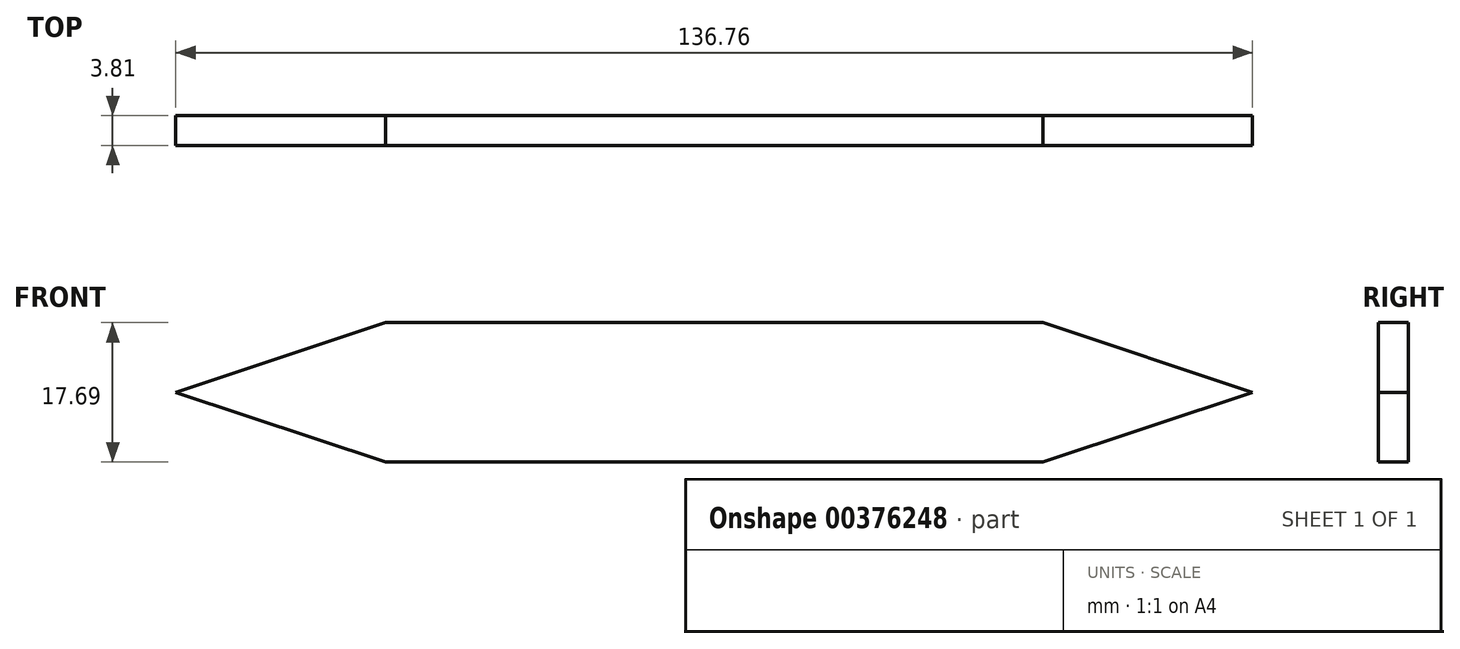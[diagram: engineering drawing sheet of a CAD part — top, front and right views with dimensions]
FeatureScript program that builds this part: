
annotation { "Feature Type Name" : "Feature", "Feature Type Description" : "" }
export const myFeature = defineFeature(function(context is Context, id is Id, definition is map)
    precondition{}
    {
        {
            var Q0;
            Q0=qCreatedBy(makeId("Front.planeOp"),FACE);
            var sketch = newSketch(context, id + "F0", { "sketchPlane" : qUnion([Q0])});
            skLineSegment(sketch, "E0.bottom", {"start": v(41.75, 0) * mm, "end": v(-41.75, 0) * mm});
            skLineSegment(sketch, "E0.top", {"start": v(41.75, 17.69) * mm, "end": v(-41.75, 17.69) * mm});
            skLineSegment(sketch, "E0.left", {"start": v(41.75, 0) * mm, "end": v(41.75, 17.69) * mm});
            skLineSegment(sketch, "E0.right", {"start": v(-41.75, 0) * mm, "end": v(-41.75, 17.69) * mm});
            skPoint(sketch, "E0.middle", {"position": v(0, 8.84) * mm});
            skLineSegment(sketch, "E1", {"start": v(-68.38, 8.84) * mm, "end": v(-41.75, 17.69) * mm});
            skLineSegment(sketch, "E2", {"start": v(-68.38, 8.84) * mm, "end": v(-41.75, 0) * mm});
            skLineSegment(sketch, "E3", {"start": v(68.38, 8.84) * mm, "end": v(41.75, 17.69) * mm});
            skLineSegment(sketch, "E4", {"start": v(41.75, 0) * mm, "end": v(68.38, 8.84) * mm});
            skSolve(sketch);
        }
        {
            var Q0;
            Q0 = qSketchRegion(id + "F0", true);
            extrude(context, id + "F1", {"entities" : qUnion([Q0]), "depth" : 3.8 * mm});
        }
    });
